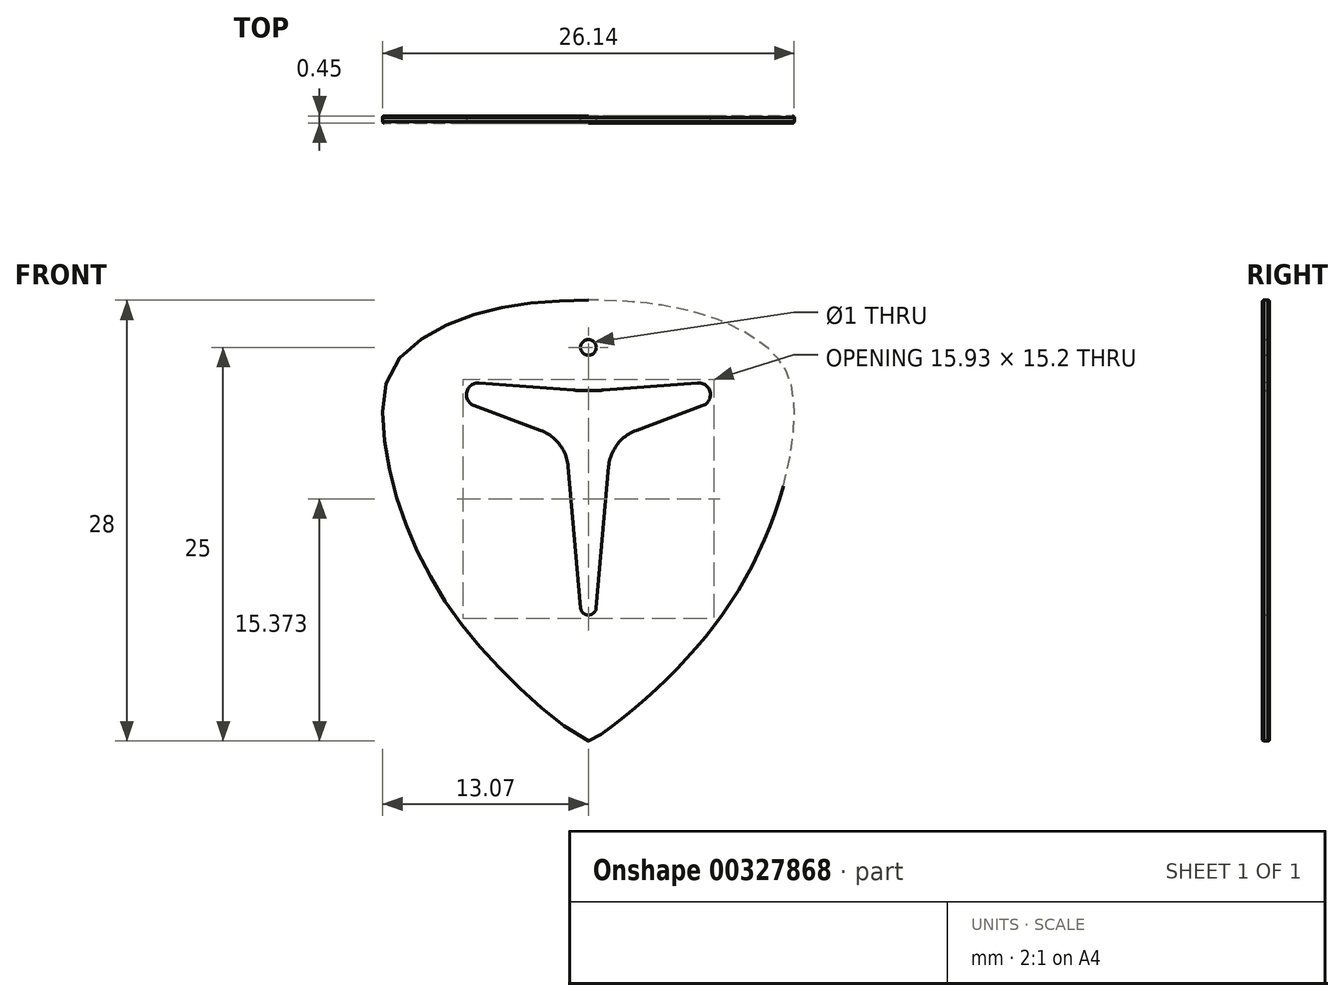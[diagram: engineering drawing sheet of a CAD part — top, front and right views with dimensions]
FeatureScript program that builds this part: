
annotation { "Feature Type Name" : "Feature", "Feature Type Description" : "" }
export const myFeature = defineFeature(function(context is Context, id is Id, definition is map)
    precondition{}
    {
        {
            var Q0;
            Q0=qCreatedBy(makeId("Front.planeOp"),FACE);
            var sketch = newSketch(context, id + "F0", { "sketchPlane" : qUnion([Q0])});
            skLineSegment(sketch, "E0", {"start": v(0, 0) * mm, "end": v(0, 6) * mm, "construction": true});
            skLineSegment(sketch, "E1", {"start": v(0, 0) * mm, "end": v(0, -22) * mm, "construction": true});
            skLineSegment(sketch, "E2", {"start": v(0, 0) * mm, "end": v(13, 0) * mm, "construction": true});
            skFitSpline(sketch, "E3", {"points": [v(0, -22) * mm, v(8.5, -14) * mm, v(13, 0) * mm, v(11, 3.25) * mm, v(0, 6) * mm], "startDerivative": vector(5.52, 0) * mm, "endDerivative": vector(-67.2, 0) * mm});
            skFitSpline(sketch, "E4.MirrorCS", {"points": [v(0, -22) * mm, v(-8.5, -14) * mm, v(-13, 0) * mm, v(-11, 3.25) * mm, v(0, 6) * mm], "startDerivative": vector(-5.52, 0) * mm, "endDerivative": vector(67.2, 0) * mm});
            skArc(sketch, "E5", {"start": v(7.26, -0.7) * mm, "mid": v(7.73, 0.16) * mm, "end": v(6.94, 0.75) * mm});
            skLineSegment(sketch, "E6", {"start": v(7.26, -0.7) * mm, "end": v(3.04, -2.27) * mm});
            skArc(sketch, "E7", {"start": v(3.04, -2.27) * mm, "mid": v(1.83, -3.17) * mm, "end": v(1.28, -4.58) * mm});
            skLineSegment(sketch, "E8", {"start": v(0.5, -13.54) * mm, "end": v(1.28, -4.58) * mm});
            skArc(sketch, "E9", {"start": v(0, -14) * mm, "mid": v(0.34, -13.87) * mm, "end": v(0.5, -13.54) * mm});
            skArc(sketch, "E10.MirrorCS", {"start": v(0, -14) * mm, "mid": v(-0.34, -13.87) * mm, "end": v(-0.5, -13.54) * mm});
            skLineSegment(sketch, "E11.MirrorCS", {"start": v(-0.5, -13.54) * mm, "end": v(-1.28, -4.58) * mm});
            skArc(sketch, "E12.MirrorCS", {"start": v(-3.04, -2.27) * mm, "mid": v(-1.83, -3.17) * mm, "end": v(-1.28, -4.58) * mm});
            skLineSegment(sketch, "E13.MirrorCS", {"start": v(-7.26, -0.7) * mm, "end": v(-3.04, -2.27) * mm});
            skArc(sketch, "E14.MirrorCS", {"start": v(-7.26, -0.7) * mm, "mid": v(-7.73, 0.16) * mm, "end": v(-6.94, 0.75) * mm});
            skLineSegment(sketch, "E15", {"start": v(6.94, 0.75) * mm, "end": v(0.96, 0.29) * mm});
            skArc(sketch, "E16", {"start": v(0, 0.25) * mm, "mid": v(0.48, 0.26) * mm, "end": v(0.96, 0.29) * mm});
            skArc(sketch, "E17.MirrorCS", {"start": v(0, 0.25) * mm, "mid": v(-0.48, 0.26) * mm, "end": v(-0.96, 0.29) * mm});
            skLineSegment(sketch, "E18.MirrorCS", {"start": v(-6.94, 0.75) * mm, "end": v(-0.96, 0.29) * mm});
            skCircle(sketch, "E19", {"center": v(0, 3) * mm, "radius": 0.5 * mm});
            skSolve(sketch);
        }
        {
            var Q0;
            Q0=qSketchRegion(id+"F0",true);
            extrude(context, id + "F1", {"entities" : qUnion([Q0]), "depth" : 0.45 * mm});
        }
        {
            var Q0;
            Q0=makeQuery(id+"F1.opExtrude","CAP_EDGE",EDGE,{"disambiguationData":[OSD([sQuery(id+"F0.wireOp",EDGE,"E5")])],"isStart":false});
            var Q1;
            Q1=makeQuery(id+"F1.opExtrude","CAP_EDGE",EDGE,{"disambiguationData":[OSD([sQuery(id+"F0.wireOp",EDGE,"E7")])],"isStart":true});
            var Q2;
            Q2=makeQuery(id+"F1.opExtrude","CAP_EDGE",EDGE,{"disambiguationData":[OSD([sQuery(id+"F0.wireOp",EDGE,"E9"),sQuery(id+"F0.wireOp",EDGE,"E10.MirrorCS")])],"isStart":false});
            var Q3;
            Q3=makeQuery(id+"F1.opExtrude","CAP_EDGE",EDGE,{"disambiguationData":[OSD([sQuery(id+"F0.wireOp",EDGE,"E14.MirrorCS")])],"isStart":false});
            var Q4;
            Q4=makeQuery(id+"F1.opExtrude","CAP_EDGE",EDGE,{"disambiguationData":[OSD([sQuery(id+"F0.wireOp",EDGE,"E5")])],"isStart":true});
            var Q5;
            Q5=makeQuery(id+"F1.opExtrude","CAP_EDGE",EDGE,{"disambiguationData":[OSD([sQuery(id+"F0.wireOp",EDGE,"E12.MirrorCS")])],"isStart":false});
            var Q6;
            Q6=makeQuery(id+"F1.opExtrude","CAP_EDGE",EDGE,{"disambiguationData":[OSD([sQuery(id+"F0.wireOp",EDGE,"E7")])],"isStart":false});
            var Q7;
            Q7=makeQuery(id+"F1.opExtrude","CAP_EDGE",EDGE,{"disambiguationData":[OSD([sQuery(id+"F0.wireOp",EDGE,"cP70XH3B-hxny-nh1n-TbyW-52Zl4TOD4HrO"),sQuery(id+"F0.wireOp",EDGE,"9cf6c757-e815-40dd-95a7-672993b90d513.MirrorCS")])],"isStart":true});
            var Q8;
            Q8=makeQuery(id+"F1.opExtrude","CAP_EDGE",EDGE,{"disambiguationData":[OSD([sQuery(id+"F0.wireOp",EDGE,"E13.MirrorCS")])],"isStart":false});
            var Q9;
            Q9=makeQuery(id+"F1.opExtrude","CAP_EDGE",EDGE,{"disambiguationData":[OSD([sQuery(id+"F0.wireOp",EDGE,"E12.MirrorCS")])],"isStart":true});
            var Q10;
            Q10=makeQuery(id+"F1.opExtrude","CAP_EDGE",EDGE,{"disambiguationData":[OSD([sQuery(id+"F0.wireOp",EDGE,"cP70XH3B-hxny-nh1n-TbyW-52Zl4TOD4HrO"),sQuery(id+"F0.wireOp",EDGE,"9cf6c757-e815-40dd-95a7-672993b90d513.MirrorCS")])],"isStart":false});
            var Q11;
            Q11=makeQuery(id+"F1.opExtrude","CAP_EDGE",EDGE,{"disambiguationData":[OSD([sQuery(id+"F0.wireOp",EDGE,"E9"),sQuery(id+"F0.wireOp",EDGE,"E10.MirrorCS")])],"isStart":true});
            var Q12;
            Q12=makeQuery(id+"F1.opExtrude","SWEPT_EDGE",EDGE,{"disambiguationData":[OSD([sQuery(id+"F0.wireOp",EDGE,"9cf6c757-e815-40dd-95a7-672993b90d513.MirrorCS"),sQuery(id+"F0.wireOp",EDGE,"E14.MirrorCS")])]});
            var Q13;
            Q13=makeQuery(id+"F1.opExtrude","CAP_EDGE",EDGE,{"disambiguationData":[OSD([sQuery(id+"F0.wireOp",EDGE,"E8")])],"isStart":true});
            var Q14;
            Q14=makeQuery(id+"F1.opExtrude","CAP_EDGE",EDGE,{"disambiguationData":[OSD([sQuery(id+"F0.wireOp",EDGE,"E11.MirrorCS")])],"isStart":false});
            var Q15;
            Q15=makeQuery(id+"F1.opExtrude","SWEPT_EDGE",EDGE,{"disambiguationData":[OSD([sQuery(id+"F0.wireOp",EDGE,"E6"),sQuery(id+"F0.wireOp",EDGE,"E7")])]});
            var Q16;
            Q16=makeQuery(id+"F1.opExtrude","SWEPT_EDGE",EDGE,{"disambiguationData":[OSD([sQuery(id+"F0.wireOp",EDGE,"E8"),sQuery(id+"F0.wireOp",EDGE,"E9")])]});
            var Q17;
            Q17=makeQuery(id+"F1.opExtrude","SWEPT_EDGE",EDGE,{"disambiguationData":[OSD([sQuery(id+"F0.wireOp",EDGE,"E13.MirrorCS"),sQuery(id+"F0.wireOp",EDGE,"E14.MirrorCS")])]});
            var Q18;
            Q18=makeQuery(id+"F1.opExtrude","SWEPT_EDGE",EDGE,{"disambiguationData":[OSD([sQuery(id+"F0.wireOp",EDGE,"E10.MirrorCS"),sQuery(id+"F0.wireOp",EDGE,"E11.MirrorCS")])]});
            var Q19;
            Q19=makeQuery(id+"F1.opExtrude","SWEPT_EDGE",EDGE,{"disambiguationData":[OSD([sQuery(id+"F0.wireOp",EDGE,"E11.MirrorCS"),sQuery(id+"F0.wireOp",EDGE,"E12.MirrorCS")])]});
            var Q20;
            Q20=makeQuery(id+"F1.opExtrude","SWEPT_EDGE",EDGE,{"disambiguationData":[OSD([sQuery(id+"F0.wireOp",EDGE,"E5"),sQuery(id+"F0.wireOp",EDGE,"E6")])]});
            var Q21;
            Q21=makeQuery(id+"F1.opExtrude","CAP_EDGE",EDGE,{"disambiguationData":[OSD([sQuery(id+"F0.wireOp",EDGE,"E14.MirrorCS")])],"isStart":true});
            var Q22;
            Q22=makeQuery(id+"F1.opExtrude","SWEPT_EDGE",EDGE,{"disambiguationData":[OSD([sQuery(id+"F0.wireOp",EDGE,"E12.MirrorCS"),sQuery(id+"F0.wireOp",EDGE,"E13.MirrorCS")])]});
            var Q23;
            Q23=makeQuery(id+"F1.opExtrude","CAP_EDGE",EDGE,{"disambiguationData":[OSD([sQuery(id+"F0.wireOp",EDGE,"E8")])],"isStart":false});
            var Q24;
            Q24=makeQuery(id+"F1.opExtrude","SWEPT_EDGE",EDGE,{"disambiguationData":[OSD([sQuery(id+"F0.wireOp",EDGE,"cP70XH3B-hxny-nh1n-TbyW-52Zl4TOD4HrO"),sQuery(id+"F0.wireOp",EDGE,"E5")])]});
            var Q25;
            Q25=makeQuery(id+"F1.opExtrude","CAP_EDGE",EDGE,{"disambiguationData":[OSD([sQuery(id+"F0.wireOp",EDGE,"E6")])],"isStart":false});
            var Q26;
            Q26=makeQuery(id+"F1.opExtrude","CAP_EDGE",EDGE,{"disambiguationData":[OSD([sQuery(id+"F0.wireOp",EDGE,"E11.MirrorCS")])],"isStart":true});
            var Q27;
            Q27=makeQuery(id+"F1.opExtrude","SWEPT_EDGE",EDGE,{"disambiguationData":[OSD([sQuery(id+"F0.wireOp",EDGE,"E7"),sQuery(id+"F0.wireOp",EDGE,"E8")])]});
            var Q28;
            Q28=makeQuery(id+"F1.opExtrude","CAP_EDGE",EDGE,{"disambiguationData":[OSD([sQuery(id+"F0.wireOp",EDGE,"E6")])],"isStart":true});
            var Q29;
            Q29=makeQuery(id+"F1.opExtrude","CAP_EDGE",EDGE,{"disambiguationData":[OSD([sQuery(id+"F0.wireOp",EDGE,"E13.MirrorCS")])],"isStart":true});
            var Q30;
            Q30=makeQuery(id+"F1.opExtrude","CAP_EDGE",EDGE,{"disambiguationData":[OSD([sQuery(id+"F0.wireOp",EDGE,"E18.MirrorCS")])],"isStart":false});
            var Q31;
            Q31=makeQuery(id+"F1.opExtrude","CAP_EDGE",EDGE,{"disambiguationData":[OSD([sQuery(id+"F0.wireOp",EDGE,"E18.MirrorCS")])],"isStart":true});
            var Q32;
            Q32=makeQuery(id+"F1.opExtrude","CAP_EDGE",EDGE,{"disambiguationData":[OSD([sQuery(id+"F0.wireOp",EDGE,"E16"),sQuery(id+"F0.wireOp",EDGE,"E17.MirrorCS")])],"isStart":false});
            var Q33;
            Q33=makeQuery(id+"F1.opExtrude","CAP_EDGE",EDGE,{"disambiguationData":[OSD([sQuery(id+"F0.wireOp",EDGE,"E16"),sQuery(id+"F0.wireOp",EDGE,"E17.MirrorCS")])],"isStart":true});
            var Q34;
            Q34=makeQuery(id+"F1.opExtrude","CAP_EDGE",EDGE,{"disambiguationData":[OSD([sQuery(id+"F0.wireOp",EDGE,"E15")])],"isStart":false});
            fillet(context, id + "F2", {"entities" : qUnion([Q0, Q1, Q2, Q3, Q4, Q5, Q6, Q7, Q8, Q9, Q10, Q11, Q12, Q13, Q14, Q15, Q16, Q17, Q18, Q19, Q20, Q21, Q22, Q23, Q24, Q25, Q26, Q27, Q28, Q29, Q30, Q31, Q32, Q33, Q34]), "radius" : (0.45 / 2) * mm, "tangentPropagation" : true, "allowEdgeOverflow" : false});
        }
        {
            var Q0;
            Q0=makeQuery(id+"F1.opExtrude","CAP_EDGE",EDGE,{"disambiguationData":[OSD([sQuery(id+"F0.wireOp",EDGE,"E3")])],"isStart":false});
            var Q1;
            Q1=makeQuery(id+"F1.opExtrude","CAP_EDGE",EDGE,{"disambiguationData":[OSD([sQuery(id+"F0.wireOp",EDGE,"E4.MirrorCS")])],"isStart":false});
            var Q2;
            Q2=makeQuery(id+"F1.opExtrude","CAP_EDGE",EDGE,{"disambiguationData":[OSD([sQuery(id+"F0.wireOp",EDGE,"E4.MirrorCS")])],"isStart":true});
            var Q3;
            Q3=makeQuery(id+"F1.opExtrude","CAP_EDGE",EDGE,{"disambiguationData":[OSD([sQuery(id+"F0.wireOp",EDGE,"E3")])],"isStart":true});
            fillet(context, id + "F3", {"entities" : qUnion([Q0, Q1, Q2, Q3]), "radius" : 0.1 * mm, "tangentPropagation" : true, "allowEdgeOverflow" : false});
        }
    });
